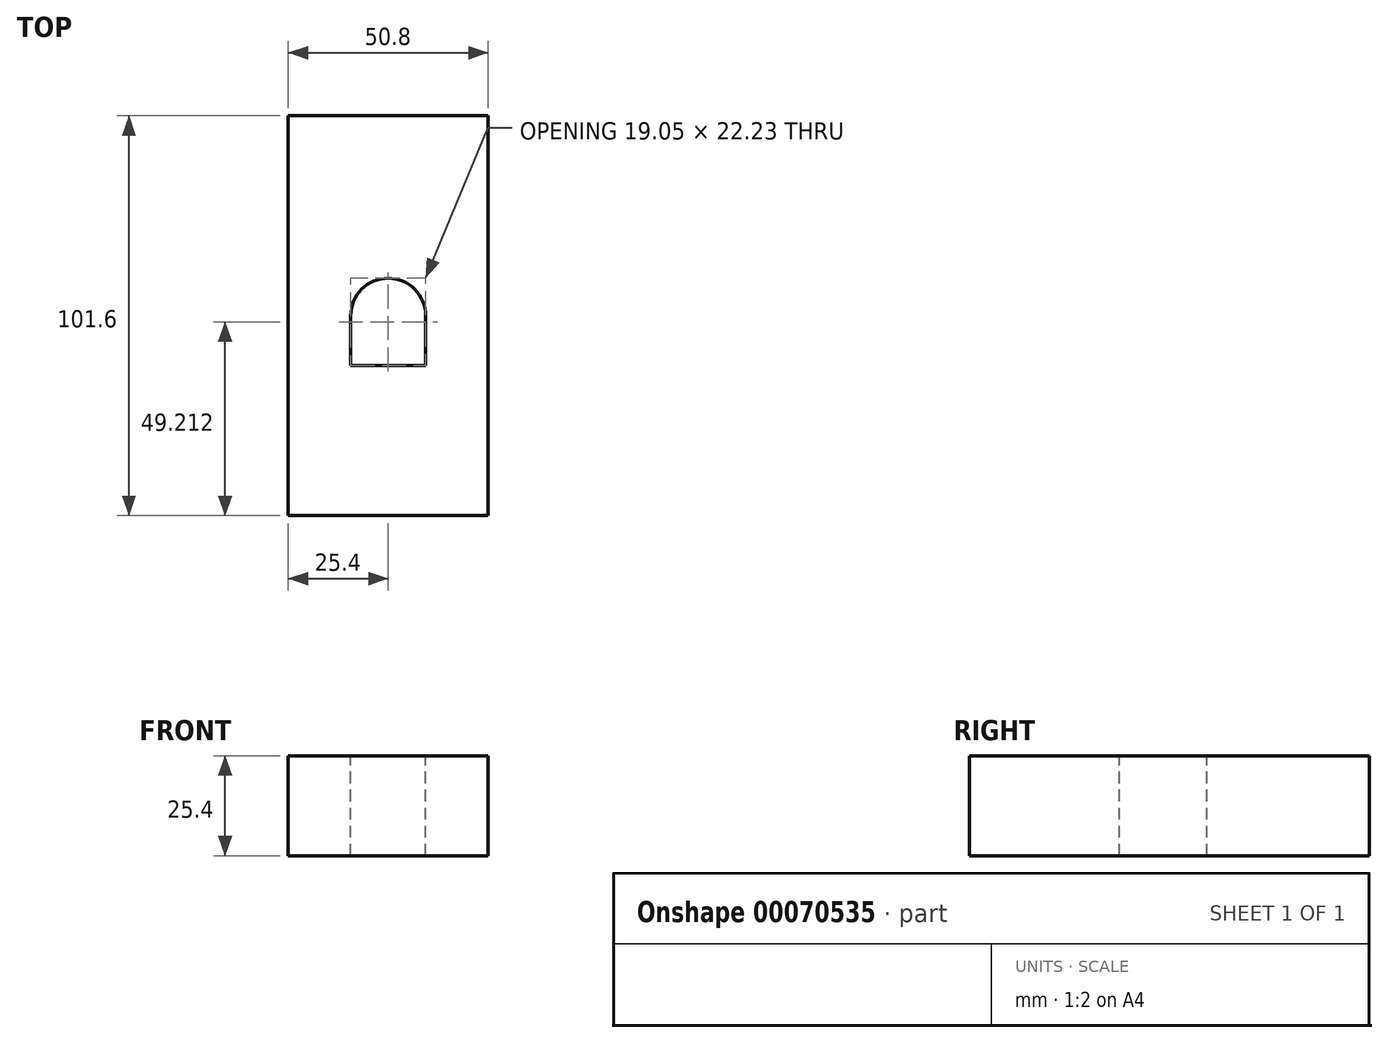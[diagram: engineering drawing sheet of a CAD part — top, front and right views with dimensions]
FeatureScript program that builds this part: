
annotation { "Feature Type Name" : "Feature", "Feature Type Description" : "" }
export const myFeature = defineFeature(function(context is Context, id is Id, definition is map)
    precondition{}
    {
        {
            var Q0;
            Q0=qCreatedBy(makeId("Front.planeOp"),FACE);
            var sketch = newSketch(context, id + "F0", { "sketchPlane" : qUnion([Q0])});
            skLineSegment(sketch, "E0.bottom", {"start": v(0, 0) * mm, "end": v(50.8, 0) * mm});
            skLineSegment(sketch, "E0.top", {"start": v(0, 25.4) * mm, "end": v(50.8, 25.4) * mm});
            skLineSegment(sketch, "E0.left", {"start": v(0, 0) * mm, "end": v(0, 25.4) * mm});
            skLineSegment(sketch, "E0.right", {"start": v(50.8, 0) * mm, "end": v(50.8, 25.4) * mm});
            skSolve(sketch);
        }
        {
            var Q0;
            Q0 = qSketchRegion(id + "F0", true);
            extrude(context, id + "F1", {"entities" : qUnion([Q0]), "depth" : 101.6 * mm});
        }
        {
            var Q0;
            Q0=makeQuery(id+"F1.opExtrude","SWEPT_FACE",FACE,{"disambiguationData":[OSD([sQuery(id+"F0.wireOp",EDGE,"E0.top")])]});
            var sketch = newSketch(context, id + "F2", { "sketchPlane" : qUnion([Q0])});
            skPoint(sketch, "E1.oppositeSnap0", {"position": v(0, -50.8) * mm});
            skLineSegment(sketch, "E2", {"start": v(0, -50.8) * mm, "end": v(50.8, -50.8) * mm, "construction": true});
            skPoint(sketch, "E3", {"position": v(25.4, -50.8) * mm});
            skLineSegment(sketch, "E4.top", {"start": v(15.87, -63.5) * mm, "end": v(34.93, -63.5) * mm});
            skLineSegment(sketch, "E4.left", {"start": v(15.88, -50.8) * mm, "end": v(15.88, -63.5) * mm});
            skLineSegment(sketch, "E4.right", {"start": v(34.93, -50.8) * mm, "end": v(34.93, -63.5) * mm});
            skLineSegment(sketch, "E5", {"start": v(25.4, -63.5) * mm, "end": v(25.4, -50.8) * mm, "construction": true});
            skArc(sketch, "E6", {"start": v(34.93, -50.8) * mm, "mid": v(25.4, -41.28) * mm, "end": v(15.88, -50.8) * mm});
            skSolve(sketch);
        }
        {
            var Q0;
            Q0 = qSketchRegion(id + "F2", true);
            extrude(context, id + "F3", {"entities" : qUnion([Q0]), "operationType" : NewBodyOperationType.REMOVE, "endBound" : BoundingType.THROUGH_ALL, "oppositeDirection" : true, "depth" : 25.4 * mm});
        }
    });
